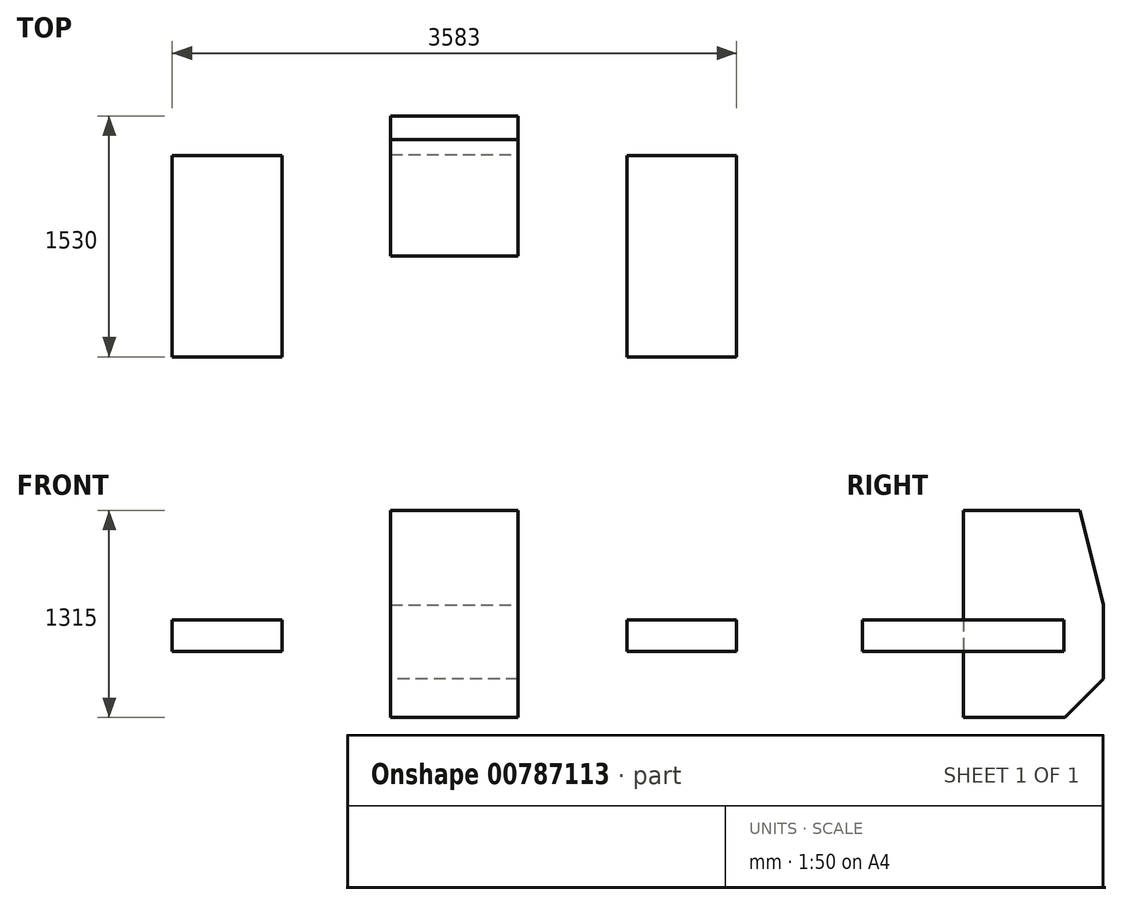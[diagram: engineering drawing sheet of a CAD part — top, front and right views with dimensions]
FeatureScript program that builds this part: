
annotation { "Feature Type Name" : "Feature", "Feature Type Description" : "" }
export const myFeature = defineFeature(function(context is Context, id is Id, definition is map)
    precondition{}
    {
        {
            var Q0;
            Q0=qCreatedBy(makeId("Front.planeOp"),FACE);
            var sketch = newSketch(context, id + "F0", { "sketchPlane" : qUnion([Q0])});
            skLineSegment(sketch, "E0.bottom", {"start": v(-1791.5, 420) * mm, "end": v(-1095, 420) * mm});
            skLineSegment(sketch, "E0.top", {"start": v(-1791.5, 620) * mm, "end": v(-1095, 620) * mm});
            skLineSegment(sketch, "E0.left", {"start": v(-1791.5, 420) * mm, "end": v(-1791.5, 620) * mm});
            skLineSegment(sketch, "E0.right", {"start": v(-1095, 420) * mm, "end": v(-1095, 620) * mm});
            skLineSegment(sketch, "E1.bottom", {"start": v(-1095, 0) * mm, "end": v(1095, 0) * mm});
            skLineSegment(sketch, "E1.top", {"start": v(-1095, 1750) * mm, "end": v(1095, 1750) * mm});
            skLineSegment(sketch, "E1.left", {"start": v(-1095, 0) * mm, "end": v(-1095, 1750) * mm});
            skLineSegment(sketch, "E1.right", {"start": v(1095, 0) * mm, "end": v(1095, 1750) * mm});
            skLineSegment(sketch, "E2.bottom", {"start": v(1095, 620) * mm, "end": v(1791.5, 620) * mm});
            skLineSegment(sketch, "E2.top", {"start": v(1095, 420) * mm, "end": v(1791.5, 420) * mm});
            skLineSegment(sketch, "E2.left", {"start": v(1095, 620) * mm, "end": v(1095, 420) * mm});
            skLineSegment(sketch, "E2.right", {"start": v(1791.5, 620) * mm, "end": v(1791.5, 420) * mm});
            skLineSegment(sketch, "E3", {"start": v(0, 1750) * mm, "end": v(0, 0) * mm, "construction": true});
            skSolve(sketch);
        }
        {
            var Q0;
            {var subQ6=sQuery(id+"F0.wireOp",EDGE,"E3");Q0=makeQuery(id+"F0.imprint","IMPRINT",FACE,{"disambiguationData":[TD([[makeQuery(id+"F0.imprint","IMPRINT",EDGE,{"derivedFrom":subQ6}),-1.0]])]});}
            var Q1;
            {var subQ3=sQuery(id+"F0.wireOp",EDGE,"E2.left");Q1=makeQuery(id+"F0.imprint","IMPRINT",FACE,{"disambiguationData":[TD([[makeQuery(id+"F0.imprint","IMPRINT",EDGE,{"derivedFrom":subQ3}),-1.0]])]});}
            var Q2;
            Q2=makeQuery(id+"F0.imprint","IMPRINT",FACE,{"disambiguationData":[TD([[makeQuery(id+"F0.imprint","IMPRINT",EDGE,{"derivedFrom":sQuery(id+"F0.wireOp",EDGE,"E2.bottom")}),-1.0]])]});
            var Q3;
            {var subQ0=sQuery(id+"F0.wireOp",EDGE,"E0.bottom");Q3=makeQuery(id+"F0.imprint","IMPRINT",FACE,{"disambiguationData":[TD([[makeQuery(id+"F0.imprint","IMPRINT",EDGE,{"derivedFrom":subQ0}),1.0]])]});}
            extrude(context, id + "F1", {"entities" : qUnion([Q0, Q1, Q2, Q3]), "endBound" : BoundingType.SYMMETRIC, "depth" : 1280 * mm, "offsetDistance" : 25 * mm});
        }
        {
            var Q0;
            Q0=qCreatedBy(makeId("Front.planeOp"),FACE);
            var sketch = newSketch(context, id + "F2", { "sketchPlane" : qUnion([Q0])});
            skLineSegment(sketch, "E4.bottom", {"start": v(-404.5, 1315) * mm, "end": v(404.5, 1315) * mm});
            skLineSegment(sketch, "E4.top", {"start": v(-404.5, 0) * mm, "end": v(404.5, 0) * mm});
            skLineSegment(sketch, "E4.left", {"start": v(-404.5, 1315) * mm, "end": v(-404.5, 0) * mm});
            skLineSegment(sketch, "E4.right", {"start": v(404.5, 1315) * mm, "end": v(404.5, 0) * mm});
            skLineSegment(sketch, "E5", {"start": v(-404.5, 1315) * mm, "end": v(404.5, 0) * mm, "construction": true});
            skLineSegment(sketch, "E6", {"start": v(0, 0) * mm, "end": v(0, 657.5) * mm, "construction": true});
            skSolve(sketch);
        }
        {
            var Q0;
            Q0=qSketchRegion(id+"F2",true);
            extrude(context, id + "F3", {"entities" : qUnion([Q0]), "operationType" : NewBodyOperationType.ADD, "oppositeDirection" : true, "depth" : 890 * mm, "offsetDistance" : 25 * mm});
        }
        {
            var Q0;
            Q0=makeQuery(id+"F3.opExtrude","CAP_EDGE",EDGE,{"disambiguationData":[OSD([sQuery(id+"F2.wireOp",EDGE,"E4.bottom")])],"isStart":false});
            chamfer(context, id + "F4", {"entities" : qUnion([Q0]), "chamferType" : ChamferType.TWO_OFFSETS, "width1" : 600 * mm, "oppositeDirection" : false, "width2" : 150 * mm, "tangentPropagation" : true});
        }
        {
            var Q0;
            Q0=makeQuery(id+"F3.opExtrude","CAP_EDGE",EDGE,{"disambiguationData":[OSD([sQuery(id+"F2.wireOp",EDGE,"E4.top")])],"isStart":false});
            chamfer(context, id + "F5", {"entities" : qUnion([Q0]), "width" : 245 * mm, "tangentPropagation" : true});
        }
    });
